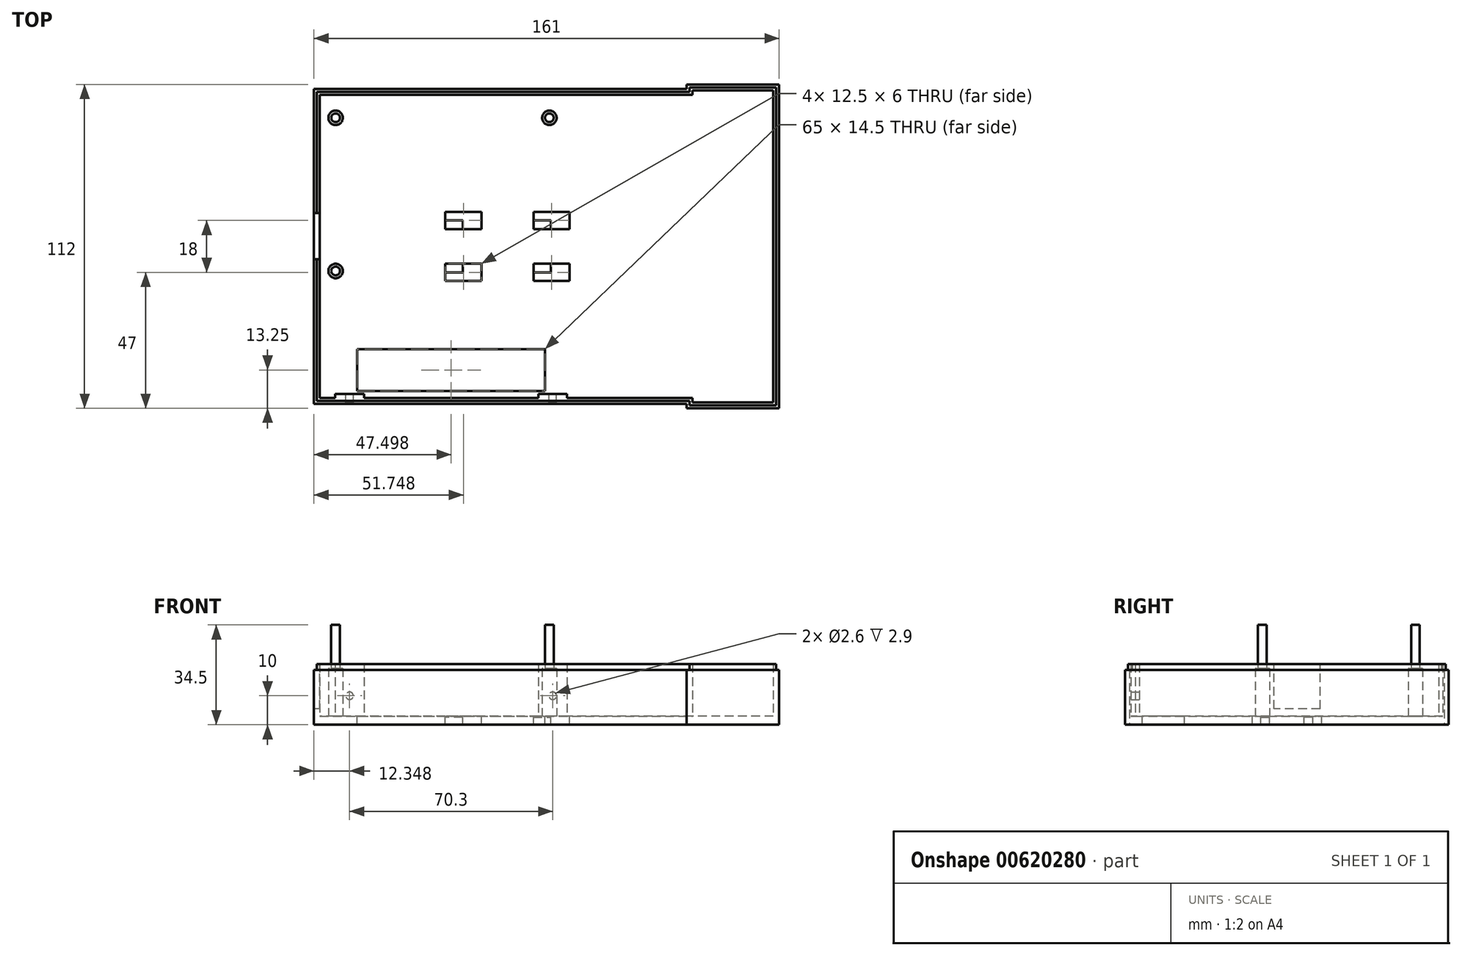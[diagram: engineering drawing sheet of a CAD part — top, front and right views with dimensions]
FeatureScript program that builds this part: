
annotation { "Feature Type Name" : "Feature", "Feature Type Description" : "" }
export const myFeature = defineFeature(function(context is Context, id is Id, definition is map)
    precondition{}
    {
        {
            var Q0;
            Q0=qCreatedBy(makeId("Top.planeOp"),FACE);
            var sketch = newSketch(context, id + "F0", { "sketchPlane" : qUnion([Q0])});
            skLineSegment(sketch, "E0", {"start": v(46.44, 56) * mm, "end": v(78.44, 56) * mm});
            skLineSegment(sketch, "E1", {"start": v(78.44, 56) * mm, "end": v(78.44, -56) * mm});
            skLineSegment(sketch, "E2", {"start": v(78.44, -56) * mm, "end": v(46.44, -56) * mm});
            skLineSegment(sketch, "E3", {"start": v(46.44, 56) * mm, "end": v(46.44, 54.5) * mm});
            skLineSegment(sketch, "E4", {"start": v(46.44, 54.5) * mm, "end": v(-82.56, 54.5) * mm});
            skLineSegment(sketch, "E5", {"start": v(-82.56, 54.5) * mm, "end": v(-82.56, -54.5) * mm});
            skLineSegment(sketch, "E6", {"start": v(-82.56, -54.5) * mm, "end": v(46.44, -54.5) * mm});
            skLineSegment(sketch, "E7", {"start": v(46.44, -54.5) * mm, "end": v(46.44, -56) * mm});
            skSolve(sketch);
        }
        {
            var Q0;
            Q0 = qSketchRegion(id + "F0", true);
            extrude(context, id + "F1", {"entities" : qUnion([Q0]), "depth" : 3 * mm, "offsetDistance" : 25 * mm});
        }
        {
            var Q0;
            Q0=makeQuery(id+"F1.opExtrude","CAP_FACE",FACE,{"disambiguationData":[OSD([sQuery(id+"F0.wireOp",EDGE,"E0"),sQuery(id+"F0.wireOp",EDGE,"E1"),sQuery(id+"F0.wireOp",EDGE,"E2"),sQuery(id+"F0.wireOp",EDGE,"E3"),sQuery(id+"F0.wireOp",EDGE,"E4"),sQuery(id+"F0.wireOp",EDGE,"E5"),sQuery(id+"F0.wireOp",EDGE,"E6"),sQuery(id+"F0.wireOp",EDGE,"E7")])],"isStart":false});
            var sketch = newSketch(context, id + "F2", { "sketchPlane" : qUnion([Q0])});
            skLineSegment(sketch, "E8", {"start": v(-80.56, 52.5) * mm, "end": v(48.44, 52.5) * mm});
            skLineSegment(sketch, "E9", {"start": v(48.44, 52.5) * mm, "end": v(48.44, 54) * mm});
            skLineSegment(sketch, "E10", {"start": v(48.44, 54) * mm, "end": v(76.44, 54) * mm});
            skLineSegment(sketch, "E11", {"start": v(76.44, 54) * mm, "end": v(76.44, -54) * mm});
            skLineSegment(sketch, "E12", {"start": v(76.44, -54) * mm, "end": v(48.44, -54) * mm});
            skLineSegment(sketch, "E13", {"start": v(48.44, -54) * mm, "end": v(48.44, -52.5) * mm});
            skLineSegment(sketch, "E14", {"start": v(48.44, -52.5) * mm, "end": v(-80.56, -52.5) * mm});
            skLineSegment(sketch, "E15", {"start": v(-80.56, -52.5) * mm, "end": v(-80.56, 52.5) * mm});
            skSolve(sketch);
        }
        {
            var Q0;
            Q0=makeQuery(id+"F2.imprint","IMPRINT",FACE,{"disambiguationData":[TD([[makeQuery(id+"F2.imprint","IMPRINT",EDGE,{"derivedFrom":sQuery(id+"F2.wireOp",EDGE,"E8")}),1.0]])]});
            extrude(context, id + "F3", {"entities" : qUnion([Q0]), "operationType" : NewBodyOperationType.ADD, "depth" : 16 * mm, "offsetDistance" : 25 * mm});
        }
        {
            var Q0;
            Q0=makeQuery(id+"F3.opExtrude","CAP_FACE",FACE,{"disambiguationData":[OSD([sQuery(id+"F0.wireOp",EDGE,"E0"),sQuery(id+"F0.wireOp",EDGE,"E1"),sQuery(id+"F0.wireOp",EDGE,"E2"),sQuery(id+"F0.wireOp",EDGE,"E3"),sQuery(id+"F0.wireOp",EDGE,"E4"),sQuery(id+"F0.wireOp",EDGE,"E5"),sQuery(id+"F0.wireOp",EDGE,"E6"),sQuery(id+"F0.wireOp",EDGE,"E7"),sQuery(id+"F2.wireOp",EDGE,"E8"),sQuery(id+"F2.wireOp",EDGE,"E9"),sQuery(id+"F2.wireOp",EDGE,"E10"),sQuery(id+"F2.wireOp",EDGE,"E11"),sQuery(id+"F2.wireOp",EDGE,"E12"),sQuery(id+"F2.wireOp",EDGE,"E13"),sQuery(id+"F2.wireOp",EDGE,"E14"),sQuery(id+"F2.wireOp",EDGE,"E15")])],"isStart":false});
            var sketch = newSketch(context, id + "F4", { "sketchPlane" : qUnion([Q0])});
            skLineSegment(sketch, "E16", {"start": v(-81.56, 53.5) * mm, "end": v(-81.56, -53.5) * mm});
            skLineSegment(sketch, "E17", {"start": v(-81.56, -53.5) * mm, "end": v(47.44, -53.5) * mm});
            skLineSegment(sketch, "E18", {"start": v(47.44, -55) * mm, "end": v(77.44, -55) * mm});
            skLineSegment(sketch, "E19", {"start": v(77.44, -55) * mm, "end": v(77.44, 55) * mm});
            skLineSegment(sketch, "E20", {"start": v(77.44, 55) * mm, "end": v(47.44, 55) * mm});
            skLineSegment(sketch, "E21", {"start": v(47.44, 55) * mm, "end": v(47.44, 53.5) * mm});
            skLineSegment(sketch, "E22", {"start": v(47.44, 53.5) * mm, "end": v(-81.56, 53.5) * mm});
            skLineSegment(sketch, "E23", {"start": v(47.44, -53.5) * mm, "end": v(47.44, -55) * mm});
            skSolve(sketch);
        }
        {
            var Q0;
            Q0=makeQuery(id+"F4.imprint","IMPRINT",FACE,{"disambiguationData":[TD([[makeQuery(id+"F4.imprint","IMPRINT",EDGE,{"derivedFrom":sQuery(id+"F4.wireOp",EDGE,"E16")}),1.0]])]});
            extrude(context, id + "F5", {"entities" : qUnion([Q0]), "operationType" : NewBodyOperationType.ADD, "depth" : 2 * mm, "offsetDistance" : 25 * mm});
        }
        {
            var Q0;
            Q0=makeQuery(id+"F1.opExtrude","CAP_FACE",FACE,{"disambiguationData":[OSD([sQuery(id+"F0.wireOp",EDGE,"E0"),sQuery(id+"F0.wireOp",EDGE,"E1"),sQuery(id+"F0.wireOp",EDGE,"E2"),sQuery(id+"F0.wireOp",EDGE,"E3"),sQuery(id+"F0.wireOp",EDGE,"E4"),sQuery(id+"F0.wireOp",EDGE,"E5"),sQuery(id+"F0.wireOp",EDGE,"E6"),sQuery(id+"F0.wireOp",EDGE,"E7")])],"isStart":false});
            var sketch = newSketch(context, id + "F6", { "sketchPlane" : qUnion([Q0])});
            skLineSegment(sketch, "E24.bottom", {"start": v(-67.56, -35.5) * mm, "end": v(-2.56, -35.5) * mm});
            skLineSegment(sketch, "E24.top", {"start": v(-67.56, -50) * mm, "end": v(-2.56, -50) * mm});
            skLineSegment(sketch, "E24.left", {"start": v(-67.56, -35.5) * mm, "end": v(-67.56, -50) * mm});
            skLineSegment(sketch, "E24.right", {"start": v(-2.56, -35.5) * mm, "end": v(-2.56, -50) * mm});
            skSolve(sketch);
        }
        {
            var Q0;
            Q0=makeQuery(id+"F6.imprint","IMPRINT",FACE,{"disambiguationData":[TD([[makeQuery(id+"F6.imprint","IMPRINT",EDGE,{"derivedFrom":sQuery(id+"F6.wireOp",EDGE,"E24.bottom")}),-1.0]])]});
            extrude(context, id + "F7", {"entities" : qUnion([Q0]), "operationType" : NewBodyOperationType.REMOVE, "endBound" : BoundingType.UP_TO_NEXT, "oppositeDirection" : true, "depth" : 25 * mm, "offsetDistance" : 25 * mm});
        }
        {
            var Q0;
            Q0=makeQuery(id+"F5.opExtrude","CAP_FACE",FACE,{"disambiguationData":[OSD([sQuery(id+"F2.wireOp",EDGE,"E8"),sQuery(id+"F2.wireOp",EDGE,"E9"),sQuery(id+"F2.wireOp",EDGE,"E10"),sQuery(id+"F2.wireOp",EDGE,"E11"),sQuery(id+"F2.wireOp",EDGE,"E12"),sQuery(id+"F2.wireOp",EDGE,"E13"),sQuery(id+"F2.wireOp",EDGE,"E14"),sQuery(id+"F2.wireOp",EDGE,"E15"),sQuery(id+"F4.wireOp",EDGE,"E16"),sQuery(id+"F4.wireOp",EDGE,"E17"),sQuery(id+"F4.wireOp",EDGE,"E18"),sQuery(id+"F4.wireOp",EDGE,"E19"),sQuery(id+"F4.wireOp",EDGE,"E20"),sQuery(id+"F4.wireOp",EDGE,"E21"),sQuery(id+"F4.wireOp",EDGE,"E22"),sQuery(id+"F4.wireOp",EDGE,"E23")])],"isStart":false});
            var sketch = newSketch(context, id + "F8", { "sketchPlane" : qUnion([Q0])});
            skLineSegment(sketch, "E25.bottom", {"start": v(-81.56, -4.5) * mm, "end": v(-80.56, -4.5) * mm});
            skLineSegment(sketch, "E25.top", {"start": v(-81.56, 11.5) * mm, "end": v(-80.56, 11.5) * mm});
            skLineSegment(sketch, "E25.left", {"start": v(-81.56, -4.5) * mm, "end": v(-81.56, 11.5) * mm});
            skLineSegment(sketch, "E25.right", {"start": v(-80.56, -4.5) * mm, "end": v(-80.56, 11.5) * mm});
            skSolve(sketch);
        }
        {
            var Q0;
            Q0=makeQuery(id+"F8.imprint","IMPRINT",FACE,{"disambiguationData":[TD([[makeQuery(id+"F8.imprint","IMPRINT",EDGE,{"derivedFrom":sQuery(id+"F8.wireOp",EDGE,"E25.bottom")}),1.0]])]});
            var Q1;
            Q1=makeQuery(id+"F3.opExtrude","CAP_FACE",FACE,{"disambiguationData":[OSD([sQuery(id+"F0.wireOp",EDGE,"E0"),sQuery(id+"F0.wireOp",EDGE,"E1"),sQuery(id+"F0.wireOp",EDGE,"E2"),sQuery(id+"F0.wireOp",EDGE,"E3"),sQuery(id+"F0.wireOp",EDGE,"E4"),sQuery(id+"F0.wireOp",EDGE,"E5"),sQuery(id+"F0.wireOp",EDGE,"E6"),sQuery(id+"F0.wireOp",EDGE,"E7"),sQuery(id+"F2.wireOp",EDGE,"E8"),sQuery(id+"F2.wireOp",EDGE,"E9"),sQuery(id+"F2.wireOp",EDGE,"E10"),sQuery(id+"F2.wireOp",EDGE,"E11"),sQuery(id+"F2.wireOp",EDGE,"E12"),sQuery(id+"F2.wireOp",EDGE,"E13"),sQuery(id+"F2.wireOp",EDGE,"E14"),sQuery(id+"F2.wireOp",EDGE,"E15")])],"isStart":false});
            extrude(context, id + "F9", {"entities" : qUnion([Q0]), "operationType" : NewBodyOperationType.REMOVE, "endBound" : BoundingType.UP_TO_SURFACE, "oppositeDirection" : true, "depth" : 25 * mm, "endBoundEntityFace" : qUnion([Q1]), "offsetDistance" : 25 * mm});
        }
        {
            var Q0;
            {var subQ0=sQuery(id+"F2.wireOp",EDGE,"E15");var subQ1=sQuery(id+"F2.wireOp",EDGE,"E14");var subQ2=sQuery(id+"F2.wireOp",EDGE,"E13");var subQ3=sQuery(id+"F2.wireOp",EDGE,"E12");var subQ4=sQuery(id+"F2.wireOp",EDGE,"E11");var subQ5=sQuery(id+"F2.wireOp",EDGE,"E10");var subQ6=sQuery(id+"F2.wireOp",EDGE,"E9");var subQ7=sQuery(id+"F2.wireOp",EDGE,"E8");var subQ8=sQuery(id+"F0.wireOp",EDGE,"E7");var subQ9=sQuery(id+"F0.wireOp",EDGE,"E6");var subQ10=sQuery(id+"F0.wireOp",EDGE,"E5");var subQ11=sQuery(id+"F0.wireOp",EDGE,"E4");var subQ12=sQuery(id+"F0.wireOp",EDGE,"E3");var subQ13=sQuery(id+"F0.wireOp",EDGE,"E2");var subQ14=sQuery(id+"F0.wireOp",EDGE,"E1");var subQ15=sQuery(id+"F0.wireOp",EDGE,"E0");Q0=makeQuery(id+"F9.boolean.opBoolean","MERGE",FACE,{"derivedFrom":[makeQuery(id+"F3.opExtrude","CAP_FACE",FACE,{"disambiguationData":[OSD([subQ15,subQ14,subQ13,subQ12,subQ11,subQ10,subQ9,subQ8,subQ7,subQ6,subQ5,subQ4,subQ3,subQ2,subQ1,subQ0])],"isStart":false}),makeQuery(id+"F9.opExtrude","CAP_FACE",FACE,{"disambiguationData":[OSD([subQ15,subQ14,subQ13,subQ12,subQ11,subQ10,subQ9,subQ8,subQ7,subQ6,subQ5,subQ4,subQ3,subQ2,subQ1,subQ0])],"isStart":false})]});}
            var sketch = newSketch(context, id + "F10", { "sketchPlane" : qUnion([Q0])});
            skLineSegment(sketch, "E26.bottom", {"start": v(-80.56, 11.5) * mm, "end": v(-82.56, 11.5) * mm});
            skLineSegment(sketch, "E26.top", {"start": v(-80.56, -4.5) * mm, "end": v(-82.56, -4.5) * mm});
            skLineSegment(sketch, "E26.left", {"start": v(-80.56, 11.5) * mm, "end": v(-80.56, -4.5) * mm});
            skLineSegment(sketch, "E26.right", {"start": v(-82.56, 11.5) * mm, "end": v(-82.56, -4.5) * mm});
            skSolve(sketch);
        }
        {
            var Q0;
            {var subQ25=sQuery(id+"F10.wireOp",EDGE,"E26.left");Q0=makeQuery(id+"F10.imprint","IMPRINT",FACE,{"disambiguationData":[TD([[makeQuery(id+"F10.imprint","IMPRINT",EDGE,{"derivedFrom":subQ25}),-1.0]])]});}
            extrude(context, id + "F11", {"entities" : qUnion([Q0]), "operationType" : NewBodyOperationType.REMOVE, "oppositeDirection" : true, "depth" : 13.5 * mm, "offsetDistance" : 25 * mm});
        }
        {
            var Q0;
            Q0=makeQuery(id+"F1.opExtrude","CAP_FACE",FACE,{"disambiguationData":[OSD([sQuery(id+"F0.wireOp",EDGE,"E0"),sQuery(id+"F0.wireOp",EDGE,"E1"),sQuery(id+"F0.wireOp",EDGE,"E2"),sQuery(id+"F0.wireOp",EDGE,"E3"),sQuery(id+"F0.wireOp",EDGE,"E4"),sQuery(id+"F0.wireOp",EDGE,"E5"),sQuery(id+"F0.wireOp",EDGE,"E6"),sQuery(id+"F0.wireOp",EDGE,"E7")])],"isStart":false});
            var sketch = newSketch(context, id + "F12", { "sketchPlane" : qUnion([Q0])});
            skLineSegment(sketch, "E27.bottom", {"start": v(2.69, -9) * mm, "end": v(-27.81, -9) * mm, "construction": true});
            skLineSegment(sketch, "E27.top", {"start": v(2.69, 9) * mm, "end": v(-27.81, 9) * mm, "construction": true});
            skLineSegment(sketch, "E27.left", {"start": v(2.69, -9) * mm, "end": v(2.69, 9) * mm, "construction": true});
            skLineSegment(sketch, "E27.right", {"start": v(-27.81, -9) * mm, "end": v(-27.81, 9) * mm, "construction": true});
            skPoint(sketch, "E27.middle", {"position": v(-12.56, 0) * mm});
            skLineSegment(sketch, "E28.bottom", {"start": v(-24.56, 6) * mm, "end": v(-31.06, 6) * mm});
            skLineSegment(sketch, "E28.top", {"start": v(-24.56, 12) * mm, "end": v(-31.06, 12) * mm});
            skLineSegment(sketch, "E28.left", {"start": v(-24.56, 6) * mm, "end": v(-24.56, 12) * mm});
            skLineSegment(sketch, "E28.right", {"start": v(-31.06, 6) * mm, "end": v(-31.06, 12) * mm});
            skPoint(sketch, "E28.middle", {"position": v(-27.81, 9) * mm});
            skLineSegment(sketch, "E29.bottom", {"start": v(5.94, 6) * mm, "end": v(-0.56, 6) * mm});
            skLineSegment(sketch, "E29.top", {"start": v(5.94, 12) * mm, "end": v(-0.56, 12) * mm});
            skLineSegment(sketch, "E29.left", {"start": v(5.94, 6) * mm, "end": v(5.94, 12) * mm});
            skLineSegment(sketch, "E29.right", {"start": v(-0.56, 6) * mm, "end": v(-0.56, 12) * mm});
            skPoint(sketch, "E29.middle", {"position": v(2.69, 9) * mm});
            skLineSegment(sketch, "E30.bottom", {"start": v(5.94, -12) * mm, "end": v(-0.56, -12) * mm});
            skLineSegment(sketch, "E30.top", {"start": v(5.94, -6) * mm, "end": v(-0.56, -6) * mm});
            skLineSegment(sketch, "E30.left", {"start": v(5.94, -12) * mm, "end": v(5.94, -6) * mm});
            skLineSegment(sketch, "E30.right", {"start": v(-0.56, -12) * mm, "end": v(-0.56, -6) * mm});
            skPoint(sketch, "E30.middle", {"position": v(2.69, -9) * mm});
            skLineSegment(sketch, "E31.bottom", {"start": v(-24.56, -12) * mm, "end": v(-31.06, -12) * mm});
            skLineSegment(sketch, "E31.top", {"start": v(-24.56, -6) * mm, "end": v(-31.06, -6) * mm});
            skLineSegment(sketch, "E31.left", {"start": v(-24.56, -12) * mm, "end": v(-24.56, -6) * mm});
            skLineSegment(sketch, "E31.right", {"start": v(-31.06, -12) * mm, "end": v(-31.06, -6) * mm});
            skPoint(sketch, "E31.middle", {"position": v(-27.81, -9) * mm});
            skLineSegment(sketch, "E32", {"start": v(-31.06, 9) * mm, "end": v(-37.06, 9) * mm});
            skLineSegment(sketch, "E33", {"start": v(-37.06, 9) * mm, "end": v(-37.06, 12) * mm});
            skLineSegment(sketch, "E34", {"start": v(-37.06, 12) * mm, "end": v(-31.06, 12) * mm});
            skLineSegment(sketch, "E35", {"start": v(-31.06, -9) * mm, "end": v(-37.06, -9) * mm});
            skLineSegment(sketch, "E36", {"start": v(-37.06, -9) * mm, "end": v(-37.06, -12) * mm});
            skLineSegment(sketch, "E37", {"start": v(-37.06, -12) * mm, "end": v(-31.06, -12) * mm});
            skLineSegment(sketch, "E38", {"start": v(-0.56, 9) * mm, "end": v(-6.56, 9) * mm});
            skLineSegment(sketch, "E39", {"start": v(-6.56, 9) * mm, "end": v(-6.56, 12) * mm});
            skLineSegment(sketch, "E40", {"start": v(-6.56, 12) * mm, "end": v(-0.56, 12) * mm});
            skLineSegment(sketch, "E41", {"start": v(-0.56, -12) * mm, "end": v(-6.56, -12) * mm});
            skLineSegment(sketch, "E42", {"start": v(-6.56, -12) * mm, "end": v(-6.56, -9) * mm});
            skLineSegment(sketch, "E43", {"start": v(-6.56, -9) * mm, "end": v(-0.56, -9) * mm});
            skSolve(sketch);
        }
        {
            var Q0;
            {var subQ2=sQuery(id+"F12.wireOp",EDGE,"E32");Q0=makeQuery(id+"F12.imprint","IMPRINT",FACE,{"disambiguationData":[TD([[makeQuery(id+"F12.imprint","IMPRINT",EDGE,{"derivedFrom":subQ2}),-1.0]])]});}
            var Q1;
            {var subQ1=sQuery(id+"F12.wireOp",EDGE,"E28.bottom");Q1=makeQuery(id+"F12.imprint","IMPRINT",FACE,{"disambiguationData":[TD([[makeQuery(id+"F12.imprint","IMPRINT",EDGE,{"derivedFrom":subQ1}),-1.0]])]});}
            var Q2;
            {var subQ2=sQuery(id+"F12.wireOp",EDGE,"E38");Q2=makeQuery(id+"F12.imprint","IMPRINT",FACE,{"disambiguationData":[TD([[makeQuery(id+"F12.imprint","IMPRINT",EDGE,{"derivedFrom":subQ2}),-1.0]])]});}
            var Q3;
            {var subQ1=sQuery(id+"F12.wireOp",EDGE,"E29.bottom");Q3=makeQuery(id+"F12.imprint","IMPRINT",FACE,{"disambiguationData":[TD([[makeQuery(id+"F12.imprint","IMPRINT",EDGE,{"derivedFrom":subQ1}),-1.0]])]});}
            var Q4;
            {var subQ1=sQuery(id+"F12.wireOp",EDGE,"E30.bottom");Q4=makeQuery(id+"F12.imprint","IMPRINT",FACE,{"disambiguationData":[TD([[makeQuery(id+"F12.imprint","IMPRINT",EDGE,{"derivedFrom":subQ1}),-1.0]])]});}
            var Q5;
            {var subQ0=sQuery(id+"F12.wireOp",EDGE,"E41");Q5=makeQuery(id+"F12.imprint","IMPRINT",FACE,{"disambiguationData":[TD([[makeQuery(id+"F12.imprint","IMPRINT",EDGE,{"derivedFrom":subQ0}),-1.0]])]});}
            var Q6;
            {var subQ1=sQuery(id+"F12.wireOp",EDGE,"E31.bottom");Q6=makeQuery(id+"F12.imprint","IMPRINT",FACE,{"disambiguationData":[TD([[makeQuery(id+"F12.imprint","IMPRINT",EDGE,{"derivedFrom":subQ1}),-1.0]])]});}
            var Q7;
            {var subQ2=sQuery(id+"F12.wireOp",EDGE,"E35");Q7=makeQuery(id+"F12.imprint","IMPRINT",FACE,{"disambiguationData":[TD([[makeQuery(id+"F12.imprint","IMPRINT",EDGE,{"derivedFrom":subQ2}),1.0]])]});}
            extrude(context, id + "F13", {"entities" : qUnion([Q0, Q1, Q2, Q3, Q4, Q5, Q6, Q7]), "operationType" : NewBodyOperationType.REMOVE, "endBound" : BoundingType.UP_TO_NEXT, "oppositeDirection" : true, "depth" : 25 * mm, "offsetDistance" : 25 * mm});
        }
        {
            var Q0;
            Q0=makeQuery(id+"F1.opExtrude","CAP_FACE",FACE,{"disambiguationData":[OSD([sQuery(id+"F0.wireOp",EDGE,"E0"),sQuery(id+"F0.wireOp",EDGE,"E1"),sQuery(id+"F0.wireOp",EDGE,"E2"),sQuery(id+"F0.wireOp",EDGE,"E3"),sQuery(id+"F0.wireOp",EDGE,"E4"),sQuery(id+"F0.wireOp",EDGE,"E5"),sQuery(id+"F0.wireOp",EDGE,"E6"),sQuery(id+"F0.wireOp",EDGE,"E7")])],"isStart":false});
            var sketch = newSketch(context, id + "F14", { "sketchPlane" : qUnion([Q0])});
            skLineSegment(sketch, "E44.bottom", {"start": v(-37.06, 9) * mm, "end": v(-31.06, 9) * mm});
            skLineSegment(sketch, "E44.top", {"start": v(-37.06, 6) * mm, "end": v(-31.06, 6) * mm});
            skLineSegment(sketch, "E44.left", {"start": v(-37.06, 9) * mm, "end": v(-37.06, 6) * mm});
            skLineSegment(sketch, "E44.right", {"start": v(-31.06, 9) * mm, "end": v(-31.06, 6) * mm});
            skLineSegment(sketch, "E45.bottom", {"start": v(-6.56, 9) * mm, "end": v(-0.56, 9) * mm});
            skLineSegment(sketch, "E45.top", {"start": v(-6.56, 6) * mm, "end": v(-0.56, 6) * mm});
            skLineSegment(sketch, "E45.left", {"start": v(-6.56, 9) * mm, "end": v(-6.56, 6) * mm});
            skLineSegment(sketch, "E45.right", {"start": v(-0.56, 9) * mm, "end": v(-0.56, 6) * mm});
            skLineSegment(sketch, "E46.bottom", {"start": v(-6.56, -9) * mm, "end": v(-0.56, -9) * mm});
            skLineSegment(sketch, "E46.top", {"start": v(-6.56, -6) * mm, "end": v(-0.56, -6) * mm});
            skLineSegment(sketch, "E46.left", {"start": v(-6.56, -9) * mm, "end": v(-6.56, -6) * mm});
            skLineSegment(sketch, "E46.right", {"start": v(-0.56, -9) * mm, "end": v(-0.56, -6) * mm});
            skLineSegment(sketch, "E47.bottom", {"start": v(-31.06, -6) * mm, "end": v(-37.06, -6) * mm});
            skLineSegment(sketch, "E47.top", {"start": v(-31.06, -9) * mm, "end": v(-37.06, -9) * mm});
            skLineSegment(sketch, "E47.left", {"start": v(-31.06, -6) * mm, "end": v(-31.06, -9) * mm});
            skLineSegment(sketch, "E47.right", {"start": v(-37.06, -6) * mm, "end": v(-37.06, -9) * mm});
            skSolve(sketch);
        }
        {
            var Q0;
            Q0=makeQuery(id+"F14.imprint","IMPRINT",FACE,{"disambiguationData":[TD([[makeQuery(id+"F14.imprint","IMPRINT",EDGE,{"derivedFrom":sQuery(id+"F14.wireOp",EDGE,"E44.bottom")}),1.0]])]});
            var Q1;
            Q1=makeQuery(id+"F14.imprint","IMPRINT",FACE,{"disambiguationData":[TD([[makeQuery(id+"F14.imprint","IMPRINT",EDGE,{"derivedFrom":sQuery(id+"F14.wireOp",EDGE,"E45.bottom")}),1.0]])]});
            var Q2;
            Q2=makeQuery(id+"F14.imprint","IMPRINT",FACE,{"disambiguationData":[TD([[makeQuery(id+"F14.imprint","IMPRINT",EDGE,{"derivedFrom":sQuery(id+"F14.wireOp",EDGE,"E46.bottom")}),1.0]])]});
            var Q3;
            Q3=makeQuery(id+"F14.imprint","IMPRINT",FACE,{"disambiguationData":[TD([[makeQuery(id+"F14.imprint","IMPRINT",EDGE,{"derivedFrom":sQuery(id+"F14.wireOp",EDGE,"E47.bottom")}),1.0]])]});
            extrude(context, id + "F15", {"entities" : qUnion([Q0, Q1, Q2, Q3]), "operationType" : NewBodyOperationType.REMOVE, "oppositeDirection" : true, "depth" : 0.4 * mm, "offsetDistance" : 25 * mm});
        }
        {
            var Q0;
            Q0=makeQuery(id+"F1.opExtrude","CAP_FACE",FACE,{"disambiguationData":[OSD([sQuery(id+"F0.wireOp",EDGE,"E0"),sQuery(id+"F0.wireOp",EDGE,"E1"),sQuery(id+"F0.wireOp",EDGE,"E2"),sQuery(id+"F0.wireOp",EDGE,"E3"),sQuery(id+"F0.wireOp",EDGE,"E4"),sQuery(id+"F0.wireOp",EDGE,"E5"),sQuery(id+"F0.wireOp",EDGE,"E6"),sQuery(id+"F0.wireOp",EDGE,"E7")])],"isStart":false});
            var sketch = newSketch(context, id + "F16", { "sketchPlane" : qUnion([Q0])});
            skCircle(sketch, "E48", {"center": v(-75.06, 44.5) * mm, "radius": 2.5 * mm});
            skCircle(sketch, "E49", {"center": v(-1.06, 44.5) * mm, "radius": 2.5 * mm});
            skCircle(sketch, "E50", {"center": v(-75.06, -8.5) * mm, "radius": 2.5 * mm});
            skLineSegment(sketch, "E51", {"start": v(-100.04, 44.5) * mm, "end": v(64.35, 44.5) * mm, "construction": true});
            skLineSegment(sketch, "E52", {"start": v(-99.72, -8.5) * mm, "end": v(62.43, -8.5) * mm, "construction": true});
            skLineSegment(sketch, "E53", {"start": v(-75.06, 65.85) * mm, "end": v(-75.06, -11.68) * mm, "construction": true});
            skLineSegment(sketch, "E54", {"start": v(-1.06, 69.22) * mm, "end": v(-1.06, -19.3) * mm, "construction": true});
            skSolve(sketch);
        }
        {
            var Q0;
            Q0=makeQuery(id+"F16.imprint","IMPRINT",FACE,{"disambiguationData":[TD([[makeQuery(id+"F16.imprint","IMPRINT",EDGE,{"derivedFrom":sQuery(id+"F16.wireOp",EDGE,"E48")}),1.0]])]});
            var Q1;
            Q1=makeQuery(id+"F16.imprint","IMPRINT",FACE,{"disambiguationData":[TD([[makeQuery(id+"F16.imprint","IMPRINT",EDGE,{"derivedFrom":sQuery(id+"F16.wireOp",EDGE,"E50")}),1.0]])]});
            var Q2;
            Q2=makeQuery(id+"F16.imprint","IMPRINT",FACE,{"disambiguationData":[TD([[makeQuery(id+"F16.imprint","IMPRINT",EDGE,{"derivedFrom":sQuery(id+"F16.wireOp",EDGE,"E49")}),1.0]])]});
            extrude(context, id + "F17", {"entities" : qUnion([Q0, Q1, Q2]), "operationType" : NewBodyOperationType.ADD, "depth" : 16.5 * mm, "offsetDistance" : 25 * mm});
        }
        {
            var Q0;
            Q0=makeQuery(id+"F17.opExtrude","CAP_FACE",FACE,{"disambiguationData":[OSD([sQuery(id+"F16.wireOp",EDGE,"E50")])],"isStart":false});
            var sketch = newSketch(context, id + "F18", { "sketchPlane" : qUnion([Q0])});
            skCircle(sketch, "E55.0", {"center": v(-75.06, 44.5) * mm, "radius": 2.5 * mm});
            skCircle(sketch, "E56.0", {"center": v(-1.06, 44.5) * mm, "radius": 2.5 * mm});
            skCircle(sketch, "E57.0", {"center": v(-75.06, -8.5) * mm, "radius": 2.5 * mm});
            skCircle(sketch, "E58", {"center": v(-75.06, 44.5) * mm, "radius": 1.5 * mm});
            skCircle(sketch, "E59", {"center": v(-1.06, 44.5) * mm, "radius": 1.5 * mm});
            skCircle(sketch, "E60", {"center": v(-75.06, -8.5) * mm, "radius": 1.5 * mm});
            skSolve(sketch);
        }
        {
            var Q0;
            Q0=makeQuery(id+"F18.imprint","IMPRINT",FACE,{"disambiguationData":[TD([[makeQuery(id+"F18.imprint","IMPRINT",EDGE,{"derivedFrom":sQuery(id+"F18.wireOp",EDGE,"E58")}),1.0]])]});
            var Q1;
            Q1=makeQuery(id+"F18.imprint","IMPRINT",FACE,{"disambiguationData":[TD([[makeQuery(id+"F18.imprint","IMPRINT",EDGE,{"derivedFrom":sQuery(id+"F18.wireOp",EDGE,"E60")}),1.0]])]});
            var Q2;
            Q2=makeQuery(id+"F18.imprint","IMPRINT",FACE,{"disambiguationData":[TD([[makeQuery(id+"F18.imprint","IMPRINT",EDGE,{"derivedFrom":sQuery(id+"F18.wireOp",EDGE,"E59")}),1.0]])]});
            extrude(context, id + "F19", {"entities" : qUnion([Q0, Q1, Q2]), "operationType" : NewBodyOperationType.ADD, "depth" : 15 * mm, "offsetDistance" : 25 * mm});
        }
        {
            var Q0;
            Q0=makeQuery(id+"F1.opExtrude","CAP_FACE",FACE,{"disambiguationData":[OSD([sQuery(id+"F0.wireOp",EDGE,"E0"),sQuery(id+"F0.wireOp",EDGE,"E1"),sQuery(id+"F0.wireOp",EDGE,"E2"),sQuery(id+"F0.wireOp",EDGE,"E3"),sQuery(id+"F0.wireOp",EDGE,"E4"),sQuery(id+"F0.wireOp",EDGE,"E5"),sQuery(id+"F0.wireOp",EDGE,"E6"),sQuery(id+"F0.wireOp",EDGE,"E7")])],"isStart":false});
            var sketch = newSketch(context, id + "F20", { "sketchPlane" : qUnion([Q0])});
            skLineSegment(sketch, "E61", {"start": v(-35.06, -16.36) * mm, "end": v(-35.06, -54.64) * mm, "construction": true});
            skLineSegment(sketch, "E62", {"start": v(-70.21, -21.22) * mm, "end": v(-70.21, -60.22) * mm, "construction": true});
            skLineSegment(sketch, "E63", {"start": v(0.09, -19.78) * mm, "end": v(0.09, -61.2) * mm, "construction": true});
            skLineSegment(sketch, "E64.0", {"start": v(48.44, -52.5) * mm, "end": v(-80.56, -52.5) * mm, "construction": true});
            skLineSegment(sketch, "E65.bottom", {"start": v(-65.21, -52.5) * mm, "end": v(-75.21, -52.5) * mm});
            skLineSegment(sketch, "E65.top", {"start": v(-65.21, -51.1) * mm, "end": v(-75.21, -51.1) * mm});
            skLineSegment(sketch, "E65.left", {"start": v(-65.21, -52.5) * mm, "end": v(-65.21, -51.1) * mm});
            skLineSegment(sketch, "E65.right", {"start": v(-75.21, -52.5) * mm, "end": v(-75.21, -51.1) * mm});
            skPoint(sketch, "E65.middle", {"position": v(-70.21, -51.8) * mm});
            skLineSegment(sketch, "E66.bottom", {"start": v(5.09, -52.5) * mm, "end": v(-4.91, -52.5) * mm});
            skLineSegment(sketch, "E66.top", {"start": v(5.09, -51.1) * mm, "end": v(-4.91, -51.1) * mm});
            skLineSegment(sketch, "E66.left", {"start": v(5.09, -52.5) * mm, "end": v(5.09, -51.1) * mm});
            skLineSegment(sketch, "E66.right", {"start": v(-4.91, -52.5) * mm, "end": v(-4.91, -51.1) * mm});
            skPoint(sketch, "E66.middle", {"position": v(0.09, -51.8) * mm});
            skSolve(sketch);
        }
        {
            var Q0;
            Q0=makeQuery(id+"F20.imprint","IMPRINT",FACE,{"disambiguationData":[TD([[makeQuery(id+"F20.imprint","IMPRINT",EDGE,{"derivedFrom":sQuery(id+"F20.wireOp",EDGE,"E65.bottom")}),-1.0]])]});
            var Q1;
            Q1=makeQuery(id+"F20.imprint","IMPRINT",FACE,{"disambiguationData":[TD([[makeQuery(id+"F20.imprint","IMPRINT",EDGE,{"derivedFrom":sQuery(id+"F20.wireOp",EDGE,"E66.bottom")}),-1.0]])]});
            var Q2;
            Q2=makeQuery(id+"F5.opExtrude","CAP_FACE",FACE,{"disambiguationData":[OSD([sQuery(id+"F2.wireOp",EDGE,"E8"),sQuery(id+"F2.wireOp",EDGE,"E9"),sQuery(id+"F2.wireOp",EDGE,"E10"),sQuery(id+"F2.wireOp",EDGE,"E11"),sQuery(id+"F2.wireOp",EDGE,"E12"),sQuery(id+"F2.wireOp",EDGE,"E13"),sQuery(id+"F2.wireOp",EDGE,"E14"),sQuery(id+"F2.wireOp",EDGE,"E15"),sQuery(id+"F4.wireOp",EDGE,"E16"),sQuery(id+"F4.wireOp",EDGE,"E17"),sQuery(id+"F4.wireOp",EDGE,"E18"),sQuery(id+"F4.wireOp",EDGE,"E19"),sQuery(id+"F4.wireOp",EDGE,"E20"),sQuery(id+"F4.wireOp",EDGE,"E21"),sQuery(id+"F4.wireOp",EDGE,"E22"),sQuery(id+"F4.wireOp",EDGE,"E23")])],"isStart":false});
            extrude(context, id + "F21", {"entities" : qUnion([Q0, Q1]), "operationType" : NewBodyOperationType.ADD, "endBound" : BoundingType.UP_TO_SURFACE, "depth" : 25 * mm, "endBoundEntityFace" : qUnion([Q2]), "offsetDistance" : 25 * mm});
        }
        {
            var Q0;
            Q0=makeQuery(id+"F21.opExtrude","SWEPT_FACE",FACE,{"disambiguationData":[OSD([sQuery(id+"F20.wireOp",EDGE,"E66.top")])]});
            var sketch = newSketch(context, id + "F22", { "sketchPlane" : qUnion([Q0])});
            skLineSegment(sketch, "E67", {"start": v(-17.45, 10) * mm, "end": v(83.76, 10) * mm, "construction": true});
            skLineSegment(sketch, "E68", {"start": v(-0.09, 23.98) * mm, "end": v(-0.09, 1.7) * mm, "construction": true});
            skPoint(sketch, "E68.startSnap0", {"position": v(-0.09, 3) * mm});
            skLineSegment(sketch, "E69", {"start": v(70.21, 23.83) * mm, "end": v(70.21, 0.97) * mm, "construction": true});
            skCircle(sketch, "E70", {"center": v(-0.09, 10) * mm, "radius": 1.3 * mm});
            skCircle(sketch, "E71", {"center": v(70.21, 10) * mm, "radius": 1.3 * mm});
            skSolve(sketch);
        }
        {
            var Q0;
            Q0=makeQuery(id+"F22.imprint","IMPRINT",FACE,{"disambiguationData":[TD([[makeQuery(id+"F22.imprint","IMPRINT",EDGE,{"derivedFrom":sQuery(id+"F22.wireOp",EDGE,"E70")}),1.0]])]});
            var Q1;
            Q1=makeQuery(id+"F22.imprint","IMPRINT",FACE,{"disambiguationData":[TD([[makeQuery(id+"F22.imprint","IMPRINT",EDGE,{"derivedFrom":sQuery(id+"F22.wireOp",EDGE,"E71")}),1.0]])]});
            extrude(context, id + "F23", {"entities" : qUnion([Q0, Q1]), "operationType" : NewBodyOperationType.REMOVE, "oppositeDirection" : true, "depth" : 2.9 * mm, "offsetDistance" : 25 * mm});
        }
    });
